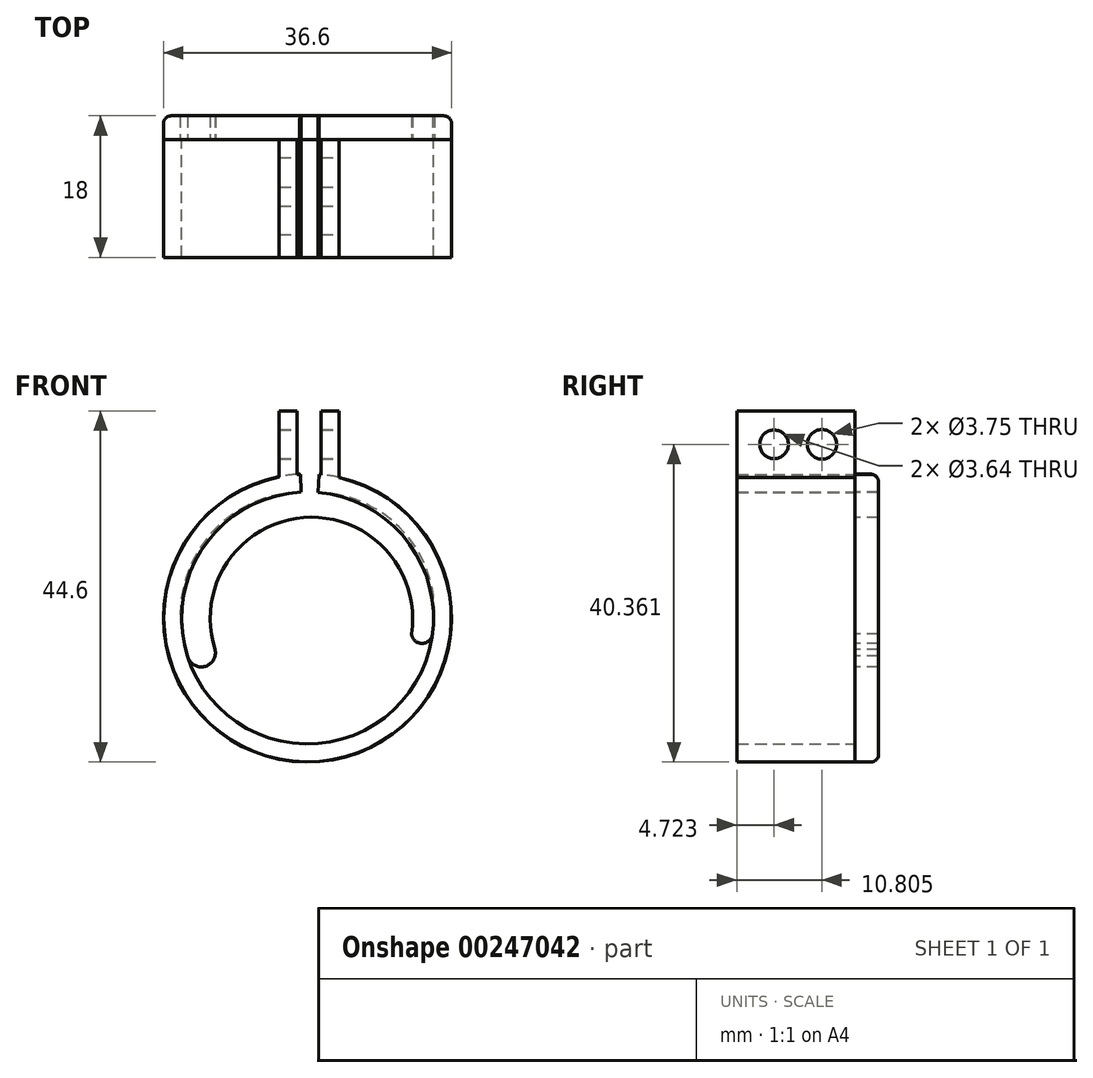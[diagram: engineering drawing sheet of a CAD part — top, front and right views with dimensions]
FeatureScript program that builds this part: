
annotation { "Feature Type Name" : "Feature", "Feature Type Description" : "" }
export const myFeature = defineFeature(function(context is Context, id is Id, definition is map)
    precondition{}
    {
        {
            var Q0;
            Q0=qCreatedBy(makeId("Front.planeOp"),FACE);
            var sketch = newSketch(context, id + "F0", { "sketchPlane" : qUnion([Q0])});
            skArc(sketch, "E0", {"start": v(-0.8, 15.98) * mm, "mid": v(-0.28, -16) * mm, "end": v(1.35, 15.94) * mm});
            skArc(sketch, "E1", {"start": v(-0.87, 18.24) * mm, "mid": v(-0.28, -18.26) * mm, "end": v(1.44, 18.2) * mm});
            skLineSegment(sketch, "E2", {"start": v(-0.87, 18.24) * mm, "end": v(-0.8, 15.98) * mm});
            skLineSegment(sketch, "E3", {"start": v(1.44, 18.2) * mm, "end": v(1.35, 15.94) * mm});
            skLineSegment(sketch, "E4.bottom", {"start": v(1.71, 15.9) * mm, "end": v(3.99, 15.9) * mm});
            skLineSegment(sketch, "E4.top", {"start": v(1.71, 26.3) * mm, "end": v(3.99, 26.3) * mm});
            skLineSegment(sketch, "E4.left", {"start": v(1.71, 15.9) * mm, "end": v(1.71, 26.3) * mm});
            skLineSegment(sketch, "E4.right", {"start": v(3.99, 15.9) * mm, "end": v(3.99, 26.3) * mm});
            skLineSegment(sketch, "E5.bottom", {"start": v(-1.32, 15.95) * mm, "end": v(-3.6, 15.95) * mm});
            skLineSegment(sketch, "E5.top", {"start": v(-1.32, 26.3) * mm, "end": v(-3.6, 26.3) * mm});
            skLineSegment(sketch, "E5.left", {"start": v(-1.32, 15.95) * mm, "end": v(-1.32, 26.3) * mm});
            skLineSegment(sketch, "E5.right", {"start": v(-3.6, 15.95) * mm, "end": v(-3.6, 26.3) * mm});
            skSolve(sketch);
        }
        {
            var Q0;
            Q0 = qSketchRegion(id + "F0", true);
            extrude(context, id + "F1", {"entities" : qUnion([Q0]), "depth" : 15 * mm});
        }
        {
            var Q0;
            Q0=makeQuery(id+"F1.opExtrude","CAP_FACE",FACE,{"disambiguationData":[OSD([sQuery(id+"F0.wireOp",EDGE,"415c3650-efae-494b-bfad-e803b6f284bd1"),sQuery(id+"F0.wireOp",EDGE,"E0"),sQuery(id+"F0.wireOp",EDGE,"SiHXEX4g-0R1F-QiyF-U0Ec-4NsxTMvAWP2O.top"),sQuery(id+"F0.wireOp",EDGE,"SiHXEX4g-0R1F-QiyF-U0Ec-4NsxTMvAWP2O.left"),sQuery(id+"F0.wireOp",EDGE,"SiHXEX4g-0R1F-QiyF-U0Ec-4NsxTMvAWP2O.right"),sQuery(id+"F0.wireOp",EDGE,"Y0LFOF78-BJo6-Jd3G-ONAf-MAevXgMQ3mVV.top"),sQuery(id+"F0.wireOp",EDGE,"Y0LFOF78-BJo6-Jd3G-ONAf-MAevXgMQ3mVV.left"),sQuery(id+"F0.wireOp",EDGE,"Y0LFOF78-BJo6-Jd3G-ONAf-MAevXgMQ3mVV.right")])],"isStart":true});
            var sketch = newSketch(context, id + "F2", { "sketchPlane" : qUnion([Q0])});
            skArc(sketch, "E6", {"start": v(11.75, -4) * mm, "mid": v(0.52, 12.76) * mm, "end": v(-13.2, -2.03) * mm});
            skArc(sketch, "E7", {"start": v(-15.87, -2.03) * mm, "mid": v(-14.54, -3.23) * mm, "end": v(-13.2, -2.03) * mm});
            skArc(sketch, "E8", {"start": v(-1.35, 15.94) * mm, "mid": v(-12.76, 10.31) * mm, "end": v(-15.87, -2.03) * mm});
            skArc(sketch, "E9", {"start": v(11.75, -4) * mm, "mid": v(13.09, -6.16) * mm, "end": v(15.25, -4.83) * mm});
            skArc(sketch, "E10", {"start": v(15.25, -4.83) * mm, "mid": v(13.38, 9.3) * mm, "end": v(0.8, 15.98) * mm});
            skArc(sketch, "E11", {"start": v(-1.46, 18.24) * mm, "mid": v(0.23, -18.3) * mm, "end": v(1, 18.27) * mm});
            skLineSegment(sketch, "E12", {"start": v(-1.46, 18.24) * mm, "end": v(-1.35, 15.94) * mm});
            skLineSegment(sketch, "E13", {"start": v(1, 18.27) * mm, "end": v(0.8, 15.98) * mm});
            skSolve(sketch);
        }
        {
            var Q0;
            Q0 = qSketchRegion(id + "F2", true);
            extrude(context, id + "F3", {"entities" : qUnion([Q0]), "operationType" : NewBodyOperationType.ADD, "depth" : 3 * mm});
        }
        {
            var Q0;
            Q0=makeQuery(id+"F3.opExtrude","CAP_EDGE",EDGE,{"disambiguationData":[OSD([sQuery(id+"F2.wireOp",EDGE,"E11")])],"isStart":false});
            fillet(context, id + "F4", {"entities" : qUnion([Q0]), "radius" : 1 * mm, "allowEdgeOverflow" : false});
        }
        {
            var Q0;
            Q0=makeQuery(id+"F1.opExtrude","SWEPT_FACE",FACE,{"disambiguationData":[OSD([sQuery(id+"F0.wireOp",EDGE,"E4.right")])]});
            var sketch = newSketch(context, id + "F5", { "sketchPlane" : qUnion([Q0])});
            skCircle(sketch, "E14", {"center": v(-10.28, 22.06) * mm, "radius": 1.82 * mm});
            skPoint(sketch, "E14.centerSnap0", {"position": v(-15, 22.06) * mm});
            skCircle(sketch, "E15", {"center": v(-4.2, 22.06) * mm, "radius": 1.87 * mm});
            skSolve(sketch);
        }
        {
            var Q0;
            Q0 = qSketchRegion(id + "F5", true);
            extrude(context, id + "F6", {"entities" : qUnion([Q0]), "operationType" : NewBodyOperationType.REMOVE, "oppositeDirection" : true, "depth" : 25 * mm});
        }
    });
